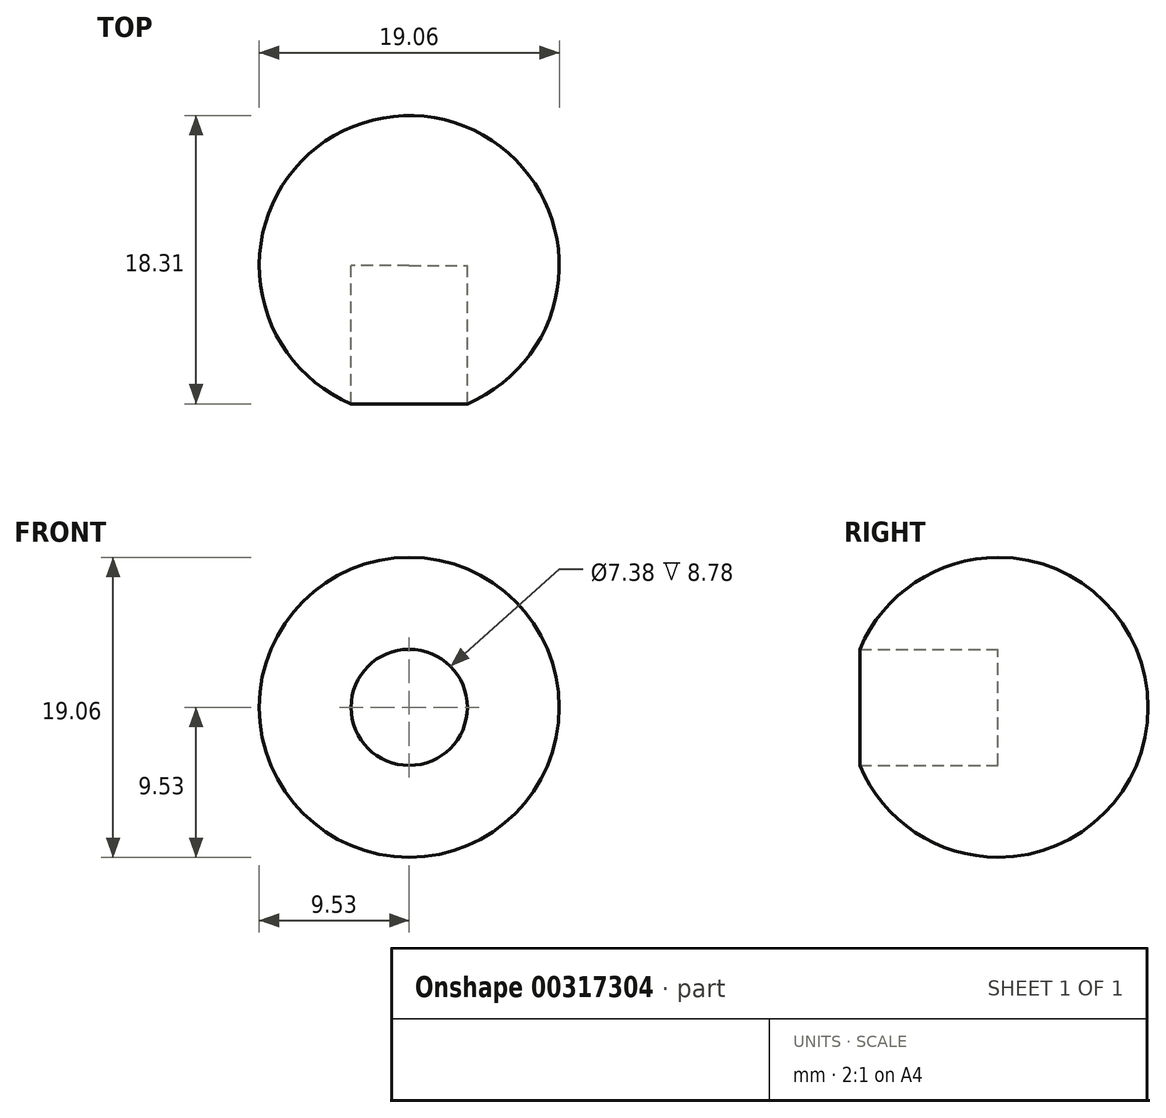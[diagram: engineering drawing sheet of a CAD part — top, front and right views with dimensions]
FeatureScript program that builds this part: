
annotation { "Feature Type Name" : "Feature", "Feature Type Description" : "" }
export const myFeature = defineFeature(function(context is Context, id is Id, definition is map)
    precondition{}
    {
        {
            var Q0;
            Q0=qCreatedBy(makeId("Front.planeOp"),FACE);
            var sketch = newSketch(context, id + "F0", { "sketchPlane" : qUnion([Q0])});
            skArc(sketch, "E0", {"start": v(0, 9.53) * mm, "mid": v(-9.53, 0) * mm, "end": v(0, -9.53) * mm});
            skLineSegment(sketch, "E1", {"start": v(0, 9.53) * mm, "end": v(0, -9.53) * mm});
            skSolve(sketch);
        }
        {
            var Q0;
            Q0=qCreatedBy(makeId("Top.planeOp"),FACE);
            var sketch = newSketch(context, id + "F1", { "sketchPlane" : qUnion([Q0])});
            skCircle(sketch, "E2", {"center": v(0, 0) * mm, "radius": 9.53 * mm});
            skSolve(sketch);
        }
        {
            var Q0;
            Q0=makeQuery(id+"F0.imprint","IMPRINT",FACE,{"disambiguationData":[TD([[makeQuery(id+"F0.imprint","IMPRINT",EDGE,{"derivedFrom":sQuery(id+"F0.wireOp",EDGE,"E0")}),1.0]])]});
            var Q1;
            Q1=sQuery(id+"F1.wireOp",EDGE,"E2");
            revolve(context, id + "F2", {"entities" : qUnion([Q0]), "axis" : qUnion([Q1]), "revolveType" : RevolveType.FULL});
        }
        {
            var Q0;
            Q0=qCreatedBy(makeId("Front.planeOp"),FACE);
            var sketch = newSketch(context, id + "F3", { "sketchPlane" : qUnion([Q0])});
            skCircle(sketch, "E3", {"center": v(0, 0) * mm, "radius": 3.7 * mm});
            skSolve(sketch);
        }
        {
            var Q0;
            Q0=makeQuery(id+"F3.imprint","IMPRINT",FACE,{"disambiguationData":[TD([[makeQuery(id+"F3.imprint","IMPRINT",EDGE,{"derivedFrom":sQuery(id+"F3.wireOp",EDGE,"E3")}),1.0]])]});
            var Q1;
            Q1=sQuery(id+"F3.wireOp",EDGE,"E3");
            extrude(context, id + "F4", {"entities" : qUnion([Q0]), "surfaceEntities" : qUnion([Q1]), "depth" : 25.4 * mm});
        }
        {
            var Q0;
            Q0=makeQuery(id+"F4.opExtrude","SWEPT_BODY",BODY,{"disambiguationData":[OSD([sQuery(id+"F3.wireOp",EDGE,"E3")])]});
            var Q1;
            Q1=makeQuery(id+"F2.opRevolve","SWEPT_BODY",BODY,{"disambiguationData":[OSD([sQuery(id+"F0.wireOp",EDGE,"E0"),sQuery(id+"F0.wireOp",EDGE,"E1")])]});
            booleanBodies(context, id + "F5", {"operationType" : BooleanOperationType.SUBTRACTION, "tools" : qUnion([Q0]), "targets" : qUnion([Q1])});
        }
    });
